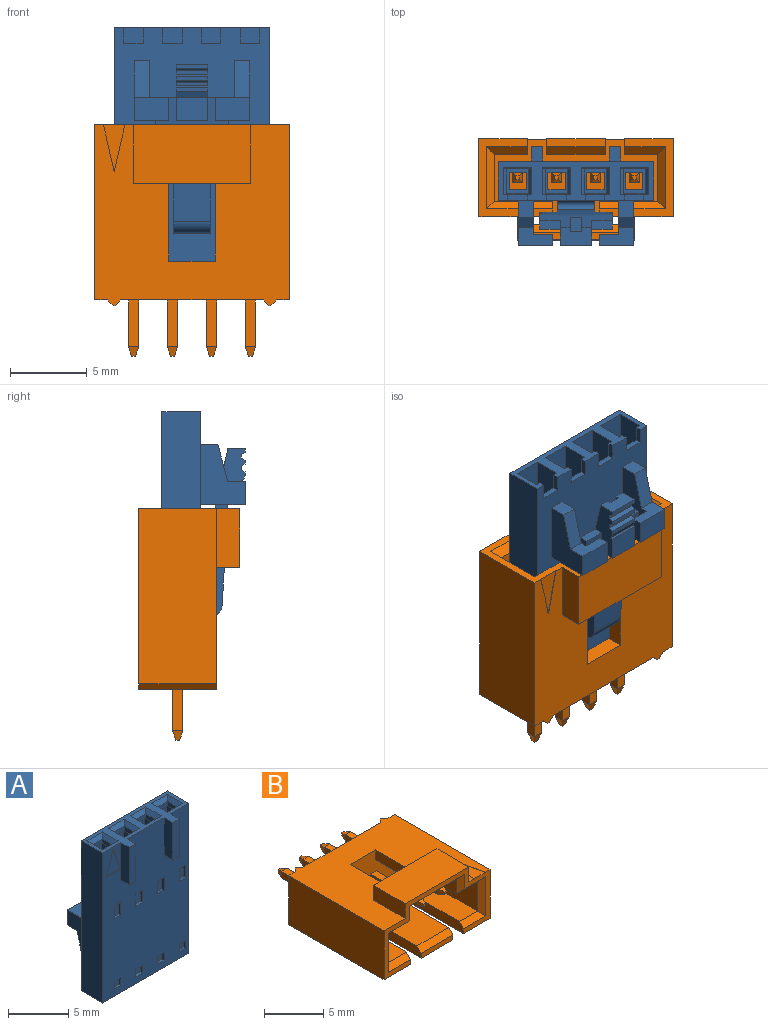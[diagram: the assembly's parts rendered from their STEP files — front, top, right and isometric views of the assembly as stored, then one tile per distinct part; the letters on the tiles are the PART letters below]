
ASSEMBLY  parts=2 mates=1
PART A: 213 faces, bbox 10.1x6.5x15.2 mm
  f0: plane 10.13x2.51mm, normal (0,0,-1), area 10.4mm2, adj f1,f2,f3,f4,f5,f32,f33,f34
  f1: plane 1.02x0.37mm, normal (1,0,0), area 0.4mm2, adj f0,f2,f38,f39
  f2: plane 8.38x1.85mm, normal (0,-1,0), area 14.3mm2, adj f0,f1,f3,f5,f7,f39,f40
  f3: plane 8.38x1.78mm, normal (1,0,0), area 14.9mm2, adj f0,f2,f4,f8
  f4: plane 8.38x1.85mm, normal (0,1,0), area 15.5mm2, adj f0,f3,f5,f9
  f5: plane 8.38x1.78mm, normal (-1,0,0), area 14.9mm2, adj f0,f2,f4,f6
  f6: plane 1.78x0.25mm, normal (-0.76,0,-0.65), area 0.6mm2, adj f5,f7,f9,f11
  f7: plane 1.85x0.25mm, normal (0,-0.96,-0.29), area 0.4mm2, adj f2,f6,f8,f12
  f8: plane 1.78x0.25mm, normal (0.76,0,-0.65), area 0.6mm2, adj f3,f7,f9,f13
  f9: plane 1.85x0.25mm, normal (0,0.96,-0.29), area 0.4mm2, adj f4,f6,f8,f10
  f10: plane 5.79x1.42mm, normal (0,1,0), area 8.2mm2, adj f9,f11,f13,f14
  f11: plane 5.79x1.63mm, normal (-1,0,0), area 9.4mm2, adj f6,f10,f12,f14
  f12: plane 5.79x1.42mm, normal (0,-1,0), area 8.2mm2, adj f7,f11,f13,f14
  f13: plane 5.79x1.63mm, normal (1,0,0), area 9.4mm2, adj f8,f10,f12,f14
  f14: plane 1.63x1.42mm, normal (0,0,-1), area 1.1mm2, adj f10,f11,f12,f13,f15,f16,f17,f18
  f15: plane 1.12x0.46mm, normal (1,0,0), area 0.5mm2, adj f14,f16,f18,f21
  f16: plane 1.12x0.46mm, normal (0,1,0), area 0.5mm2, adj f14,f15,f17,f22
  f17: plane 1.12x0.46mm, normal (-1,0,0), area 0.5mm2, adj f14,f16,f18,f23
  f18: plane 1.12x0.46mm, normal (0,-1,0), area 0.5mm2, adj f14,f15,f17,f19
  f19: plane 1.83x0.36mm, normal (0,-0.71,0.71), area 0.7mm2, adj f18,f20,f21,f23
  f20: plane 10.13x3.53mm, normal (0,0,1), area 13.7mm2, adj f19,f21,f22,f23,f24,f25,f26,f27
  f21: plane 1.83x0.36mm, normal (0.71,0,0.71), area 0.7mm2, adj f15,f19,f20,f22
  f22: plane 1.83x0.36mm, normal (0,0.71,0.71), area 0.7mm2, adj f16,f20,f21,f23
  f23: plane 1.83x0.36mm, normal (-0.71,0,0.71), area 0.7mm2, adj f17,f19,f20,f22
  f24: plane 1.83x0.36mm, normal (0.71,0,0.71), area 0.7mm2, adj f20,f25,f27,f210
  f25: plane 1.83x0.36mm, normal (0,-0.71,0.71), area 0.7mm2, adj f20,f24,f26,f211
  f26: plane 1.83x0.36mm, normal (-0.71,0,0.71), area 0.7mm2, adj f20,f25,f27,f212
  f27: plane 1.83x0.36mm, normal (0,0.71,0.71), area 0.7mm2, adj f20,f24,f26,f28
  f28: plane 1.12x0.46mm, normal (0,1,0), area 0.5mm2, adj f27,f29,f210,f212
  f29: plane 1.63x1.42mm, normal (0,0,-1), area 1.1mm2, adj f28,f30,f205,f206,f209,f210,f211,f212
  f30: plane 5.79x1.63mm, normal (1,0,0), area 9.4mm2, adj f29,f31,f205,f209
  f31: plane 1.78x0.25mm, normal (0.76,0,-0.65), area 0.6mm2, adj f30,f32,f204,f208
  f32: plane 8.38x1.78mm, normal (1,0,0), area 14.9mm2, adj f0,f31,f33,f35
  f33: plane 8.38x1.85mm, normal (0,1,0), area 15.5mm2, adj f0,f32,f34,f208
  f34: plane 8.38x1.78mm, normal (-1,0,0), area 14.9mm2, adj f0,f33,f35,f207
  f35: plane 8.38x1.85mm, normal (0,-1,0), area 14.3mm2, adj f0,f32,f34,f36,f37,f41,f204
  f36: plane 1.02x0.37mm, normal (1,0,0), area 0.4mm2, adj f0,f35,f37,f38
  f37: plane 1.27x0.37mm, normal (0,0,-1), area 0.5mm2, adj f35,f36,f38,f41
  f38: plane 15.24x10.13mm, normal (0,1,0), area 138.1mm2, adj f0,f1,f20,f36,f37,f39,f40,f41
  f39: plane 1.27x0.37mm, normal (0,0,-1), area 0.5mm2, adj f1,f2,f38,f40
  f40: plane 1.02x0.37mm, normal (-1,0,0), area 0.4mm2, adj f0,f2,f38,f39
  f41: plane 1.02x0.37mm, normal (-1,0,0), area 0.4mm2, adj f0,f35,f37,f38
  f42: plane 1.02x0.37mm, normal (1,0,0), area 0.4mm2, adj f0,f38,f43,f65
  f43: plane 8.38x1.85mm, normal (0,-1,0), area 14.3mm2, adj f0,f42,f44,f46,f48,f64,f65
  f44: plane 8.38x1.78mm, normal (1,0,0), area 14.9mm2, adj f0,f43,f45,f49
  f45: plane 8.38x1.85mm, normal (0,1,0), area 15.5mm2, adj f0,f44,f46,f50
  f46: plane 8.38x1.78mm, normal (-1,0,0), area 14.9mm2, adj f0,f43,f45,f47
  f47: plane 1.78x0.25mm, normal (-0.76,0,-0.65), area 0.6mm2, adj f46,f48,f50,f52
  f48: plane 1.85x0.25mm, normal (0,-0.96,-0.29), area 0.4mm2, adj f43,f47,f49,f53
  f49: plane 1.78x0.25mm, normal (0.76,0,-0.65), area 0.6mm2, adj f44,f48,f50,f54
  f50: plane 1.85x0.25mm, normal (0,0.96,-0.29), area 0.4mm2, adj f45,f47,f49,f51
  f51: plane 5.79x1.42mm, normal (0,1,0), area 8.2mm2, adj f50,f52,f54,f55
  f52: plane 5.79x1.63mm, normal (-1,0,0), area 9.4mm2, adj f47,f51,f53,f55
  f53: plane 5.79x1.42mm, normal (0,-1,0), area 8.2mm2, adj f48,f52,f54,f55
  f54: plane 5.79x1.63mm, normal (1,0,0), area 9.4mm2, adj f49,f51,f53,f55
  f55: plane 1.63x1.42mm, normal (0,0,-1), area 1.1mm2, adj f51,f52,f53,f54,f56,f57,f58,f59
  f56: plane 1.12x0.46mm, normal (1,0,0), area 0.5mm2, adj f55,f57,f59,f63
  f57: plane 1.12x0.46mm, normal (0,1,0), area 0.5mm2, adj f55,f56,f58,f62
  f58: plane 1.12x0.46mm, normal (-1,0,0), area 0.5mm2, adj f55,f57,f59,f61
  f59: plane 1.12x0.46mm, normal (0,-1,0), area 0.5mm2, adj f55,f56,f58,f60
  f60: plane 1.83x0.36mm, normal (0,-0.71,0.71), area 0.7mm2, adj f20,f59,f61,f63
  f61: plane 1.83x0.36mm, normal (-0.71,0,0.71), area 0.7mm2, adj f20,f58,f60,f62
  f62: plane 1.83x0.36mm, normal (0,0.71,0.71), area 0.7mm2, adj f20,f57,f61,f63
  f63: plane 1.83x0.36mm, normal (0.71,0,0.71), area 0.7mm2, adj f20,f56,f60,f62
  f64: plane 1.02x0.37mm, normal (-1,0,0), area 0.4mm2, adj f0,f38,f43,f65
  f65: plane 1.27x0.37mm, normal (0,0,-1), area 0.5mm2, adj f38,f42,f43,f64
  f66: plane 1.02x0.37mm, normal (1,0,0), area 0.4mm2, adj f0,f38,f67,f89
  f67: plane 8.38x1.85mm, normal (0,-1,0), area 14.3mm2, adj f0,f66,f68,f70,f72,f88,f89
  f68: plane 8.38x1.78mm, normal (1,0,0), area 14.9mm2, adj f0,f67,f69,f73
  f69: plane 8.38x1.85mm, normal (0,1,0), area 15.5mm2, adj f0,f68,f70,f74
  f70: plane 8.38x1.78mm, normal (-1,0,0), area 14.9mm2, adj f0,f67,f69,f71
  f71: plane 1.78x0.25mm, normal (-0.76,0,-0.65), area 0.6mm2, adj f70,f72,f74,f76
  f72: plane 1.85x0.25mm, normal (0,-0.96,-0.29), area 0.4mm2, adj f67,f71,f73,f77
  f73: plane 1.78x0.25mm, normal (0.76,0,-0.65), area 0.6mm2, adj f68,f72,f74,f78
  f74: plane 1.85x0.25mm, normal (0,0.96,-0.29), area 0.4mm2, adj f69,f71,f73,f75
  f75: plane 5.79x1.42mm, normal (0,1,0), area 8.2mm2, adj f74,f76,f78,f79
  f76: plane 5.79x1.63mm, normal (-1,0,0), area 9.4mm2, adj f71,f75,f77,f79
  f77: plane 5.79x1.42mm, normal (0,-1,0), area 8.2mm2, adj f72,f76,f78,f79
  f78: plane 5.79x1.63mm, normal (1,0,0), area 9.4mm2, adj f73,f75,f77,f79
  f79: plane 1.63x1.42mm, normal (0,0,-1), area 1.1mm2, adj f75,f76,f77,f78,f80,f81,f82,f83
  f80: plane 1.12x0.46mm, normal (1,0,0), area 0.5mm2, adj f79,f81,f83,f87
  f81: plane 1.12x0.46mm, normal (0,1,0), area 0.5mm2, adj f79,f80,f82,f86
  f82: plane 1.12x0.46mm, normal (-1,0,0), area 0.5mm2, adj f79,f81,f83,f85
  f83: plane 1.12x0.46mm, normal (0,-1,0), area 0.5mm2, adj f79,f80,f82,f84
  f84: plane 1.83x0.36mm, normal (0,-0.71,0.71), area 0.7mm2, adj f20,f83,f85,f87
  f85: plane 1.83x0.36mm, normal (-0.71,0,0.71), area 0.7mm2, adj f20,f82,f84,f86
  f86: plane 1.83x0.36mm, normal (0,0.71,0.71), area 0.7mm2, adj f20,f81,f85,f87
  f87: plane 1.83x0.36mm, normal (0.71,0,0.71), area 0.7mm2, adj f20,f80,f84,f86
  f88: plane 1.02x0.37mm, normal (-1,0,0), area 0.4mm2, adj f0,f38,f67,f89
  f89: plane 1.27x0.37mm, normal (0,0,-1), area 0.5mm2, adj f38,f66,f67,f88
  f90: plane 15.24x2.51mm, normal (1,0,0), area 38.3mm2, adj f0,f20,f38,f91
  f91: plane 15.24x10.13mm, normal (0,-1,0), area 140.4mm2, adj f0,f20,f90,f92,f93,f94,f95,f98
  f92: plane 0.76x0.25mm, normal (0,0,1), area 0.2mm2, adj f91,f93,f95,f96
  f93: plane 1.27x0.25mm, normal (1,0,0), area 0.3mm2, adj f91,f92,f94,f96
  f94: plane 0.76x0.25mm, normal (0,0,-1), area 0.2mm2, adj f91,f93,f95,f96
  f95: plane 1.27x0.25mm, normal (-1,0,0), area 0.3mm2, adj f91,f92,f94,f96
  f96: plane 1.27x0.76mm, normal (0,-1,0), area 1mm2, adj f92,f93,f94,f95
  f97: plane 0.76x0.76mm, normal (0,-1,0), area 0.6mm2, adj f98,f99,f100,f101
  f98: plane 0.76x0.25mm, normal (0,0,1), area 0.2mm2, adj f91,f97,f99,f101
  f99: plane 0.76x0.25mm, normal (1,0,0), area 0.2mm2, adj f91,f97,f98,f100
  f100: plane 0.76x0.25mm, normal (0,0,-1), area 0.2mm2, adj f91,f97,f99,f101
  f101: plane 0.76x0.25mm, normal (-1,0,0), area 0.2mm2, adj f91,f97,f98,f100
  f102: plane 0.76x0.25mm, normal (0,0,1), area 0.2mm2, adj f91,f103,f105,f106
  f103: plane 1.27x0.25mm, normal (1,0,0), area 0.3mm2, adj f91,f102,f104,f106
  f104: plane 0.76x0.25mm, normal (0,0,-1), area 0.2mm2, adj f91,f103,f105,f106
  f105: plane 1.27x0.25mm, normal (-1,0,0), area 0.3mm2, adj f91,f102,f104,f106
  f106: plane 1.27x0.76mm, normal (0,-1,0), area 1mm2, adj f102,f103,f104,f105
  f107: plane 0.76x0.76mm, normal (0,-1,0), area 0.6mm2, adj f108,f109,f110,f111
  f108: plane 0.76x0.25mm, normal (0,0,1), area 0.2mm2, adj f91,f107,f109,f111
  f109: plane 0.76x0.25mm, normal (1,0,0), area 0.2mm2, adj f91,f107,f108,f110
  f110: plane 0.76x0.25mm, normal (0,0,-1), area 0.2mm2, adj f91,f107,f109,f111
  f111: plane 0.76x0.25mm, normal (-1,0,0), area 0.2mm2, adj f91,f107,f108,f110
  f112: plane 0.76x0.25mm, normal (0,0,1), area 0.2mm2, adj f91,f113,f115,f116
  f113: plane 1.27x0.25mm, normal (1,0,0), area 0.3mm2, adj f91,f112,f114,f116
  f114: plane 0.76x0.25mm, normal (0,0,-1), area 0.2mm2, adj f91,f113,f115,f116
  f115: plane 1.27x0.25mm, normal (-1,0,0), area 0.3mm2, adj f91,f112,f114,f116
  f116: plane 1.27x0.76mm, normal (0,-1,0), area 1mm2, adj f112,f113,f114,f115
  f117: plane 0.76x0.76mm, normal (0,-1,0), area 0.6mm2, adj f118,f119,f120,f121
  f118: plane 0.76x0.25mm, normal (0,0,1), area 0.2mm2, adj f91,f117,f119,f121
  f119: plane 0.76x0.25mm, normal (1,0,0), area 0.2mm2, adj f91,f117,f118,f120
  f120: plane 0.76x0.25mm, normal (0,0,-1), area 0.2mm2, adj f91,f117,f119,f121
  f121: plane 0.76x0.25mm, normal (-1,0,0), area 0.2mm2, adj f91,f117,f118,f120
  f122: plane 0.76x0.25mm, normal (0,0,1), area 0.2mm2, adj f91,f123,f125,f126
  f123: plane 1.27x0.25mm, normal (1,0,0), area 0.3mm2, adj f91,f122,f124,f126
  f124: plane 0.76x0.25mm, normal (0,0,-1), area 0.2mm2, adj f91,f123,f125,f126
  f125: plane 1.27x0.25mm, normal (-1,0,0), area 0.3mm2, adj f91,f122,f124,f126
  f126: plane 1.27x0.76mm, normal (0,-1,0), area 1mm2, adj f122,f123,f124,f125
  f127: plane 0.76x0.76mm, normal (0,-1,0), area 0.6mm2, adj f128,f129,f130,f131
  f128: plane 0.76x0.25mm, normal (0,0,1), area 0.2mm2, adj f91,f127,f129,f131
  f129: plane 0.76x0.25mm, normal (1,0,0), area 0.2mm2, adj f91,f127,f128,f130
  f130: plane 0.76x0.25mm, normal (0,0,-1), area 0.2mm2, adj f91,f127,f129,f131
  f131: plane 0.76x0.25mm, normal (-1,0,0), area 0.2mm2, adj f91,f127,f128,f130
  f132: plane 3.81x1.02mm, normal (1,0,0), area 3.9mm2, adj f20,f91,f133,f135
  f133: plane 1.02x0.76mm, normal (0,0,-1), area 0.8mm2, adj f91,f132,f134,f135
  f134: plane 3.81x1.02mm, normal (-1,0,0), area 3.9mm2, adj f20,f91,f133,f135
  f135: plane 3.81x0.76mm, normal (0,-1,0), area 2.9mm2, adj f20,f132,f133,f134
  f136: plane 15.24x2.51mm, normal (-1,0,0), area 38.3mm2, adj f0,f20,f38,f91
  f137: plane 3.81x1.02mm, normal (-1,0,0), area 3.9mm2, adj f20,f91,f138,f140
  f138: plane 3.81x0.76mm, normal (0,-1,0), area 2.9mm2, adj f20,f137,f139,f140
  f139: plane 3.81x1.02mm, normal (1,0,0), area 3.9mm2, adj f20,f91,f138,f140
  f140: plane 1.02x0.76mm, normal (0,0,-1), area 0.8mm2, adj f91,f137,f138,f139
  f141: plane 2.54x0.81mm, normal (0.95,0,-0.3), area 0.1mm2, adj f91,f142,f143,f144
  f142: plane 2.54x0.81mm, normal (-0.95,0,-0.3), area 0.1mm2, adj f91,f141,f143,f144
  f143: plane 1.63x0.05mm, normal (0,0,1), area 0.1mm2, adj f91,f141,f142,f144
  f144: plane 2.54x1.63mm, normal (0,-1,0), area 2.1mm2, adj f141,f142,f143
  f145: plane 3.94x2.24mm, normal (-1,0,0), area 6.9mm2, adj f38,f146,f147,f149,f152,f153
  f146: plane 1.52x1.26mm, normal (0,-1,0), area 1.9mm2, adj f145,f147,f149,f150
  f147: plane 2.25x1.14mm, normal (0,0,-1), area 2mm2, adj f145,f146,f148,f150,f151,f152
  f148: plane 2.25x1.52mm, normal (0,1,0), area 3.4mm2, adj f147,f149,f150,f151
  f149: plane 2.92x2.25mm, normal (0,0,1), area 3.8mm2, adj f38,f145,f146,f148,f150,f151
  f150: plane 1.52x0.69mm, normal (-1,0,0), area 1mm2, adj f146,f147,f148,f149
  f151: plane 3.94x2.92mm, normal (1,0,0), area 8mm2, adj f38,f147,f148,f149,f152,f153
  f152: plane 2.41x0.99mm, normal (0,0.97,-0.25), area 2.5mm2, adj f145,f147,f151,f153
  f153: plane 1.14x0.99mm, normal (0,0,-1), area 1.1mm2, adj f38,f145,f151,f152
  f154: plane 3.94x2.24mm, normal (1,0,0), area 6.9mm2, adj f38,f155,f156,f158,f161,f162
  f155: plane 1.52x1.26mm, normal (0,-1,0), area 1.9mm2, adj f154,f156,f158,f159
  f156: plane 2.92x2.25mm, normal (0,0,1), area 3.8mm2, adj f38,f154,f155,f157,f159,f160
  f157: plane 2.25x1.52mm, normal (0,1,0), area 3.4mm2, adj f156,f158,f159,f160
  f158: plane 2.25x1.14mm, normal (0,0,-1), area 2mm2, adj f154,f155,f157,f159,f160,f162
  f159: plane 1.52x0.69mm, normal (1,0,0), area 1mm2, adj f155,f156,f157,f158
  f160: plane 3.94x2.92mm, normal (-1,0,0), area 8mm2, adj f38,f156,f157,f158,f161,f162
  f161: plane 1.14x0.99mm, normal (0,0,-1), area 1.1mm2, adj f38,f154,f160,f162
  f162: plane 2.41x0.99mm, normal (0,0.97,-0.25), area 2.5mm2, adj f154,f158,f160,f161
  f163: plane 4.01x1.6mm, normal (-1,0,0), area 3.9mm2, adj f38,f164,f171,f173,f174,f176,f177
  f164: plane 8.07x4.75mm, normal (0,1,0.06), area 25.1mm2, adj f163,f165,f166,f167,f168,f170,f171,f172
  f165: plane 2.03x0.64mm, normal (0,0,-1), area 1.3mm2, adj f164,f166,f168,f169
  f166: plane 1.22x0.71mm, normal (1,0,0), area 0.6mm2, adj f164,f165,f167,f169
  f167: plane 2.03x0.71mm, normal (0,0.68,0.73), area 2mm2, adj f164,f166,f168,f169
  f168: plane 1.22x0.71mm, normal (-1,0,0), area 0.6mm2, adj f164,f165,f167,f169
  f169: plane 2.03x0.56mm, normal (0,1,0), area 1.1mm2, adj f165,f166,f167,f168
  f170: plane 0.87x0.51mm, normal (-0.71,0,0.71), area 0.6mm2, adj f164,f171,f173,f203
  f171: plane 0.84x0.65mm, normal (0,0,1), area 0.5mm2, adj f163,f164,f170,f173
  f172: plane 0.84x0.65mm, normal (0,0,1), area 0.5mm2, adj f164,f173,f175,f178
  f173: plane 5.94x4.75mm, normal (0,-1,-0.06), area 21.9mm2, adj f163,f170,f171,f172,f174,f175,f178,f179
  f174: cylinder r=0.3mm len=2.44mm, axis (1,0,0), area 2.3mm2, adj f38,f163,f173,f175
  f175: plane 4.01x1.6mm, normal (1,0,0), area 3.9mm2, adj f38,f164,f172,f173,f174,f176,f177
  f176: plane 2.44x0.6mm, normal (0,0,1), area 1.5mm2, adj f38,f163,f175,f177
  f177: cylinder r=0.81mm len=2.44mm, axis (1,0,0), area 3mm2, adj f163,f164,f175,f176
  f178: plane 0.87x0.51mm, normal (0.71,0,0.71), area 0.6mm2, adj f164,f172,f173,f179
  f179: plane 4.32x1.09mm, normal (1,0,0), area 3.4mm2, adj f164,f173,f178,f181,f183
  f180: plane 1.36x0.58mm, normal (0,0,-1), area 0.8mm2, adj f164,f182,f183,f203
  f181: plane 1.36x0.58mm, normal (0,0,-1), area 0.8mm2, adj f164,f179,f183,f189
  f182: plane 3.68x1.62mm, normal (-1,0,0), area 4.4mm2, adj f164,f180,f183,f184,f190,f191,f192,f193
  f183: plane 4.75x3.68mm, normal (0,-0.98,-0.22), area 9.5mm2, adj f173,f179,f180,f181,f182,f184,f185,f187
  f184: plane 2.03x1.13mm, normal (0,0,-1), area 2.1mm2, adj f182,f183,f185,f186,f187,f189,f202
  f185: plane 3.05x0.93mm, normal (-1,0,0), area 1.8mm2, adj f183,f184,f186,f188
  f186: plane 3.05x0.76mm, normal (0,-1,0), area 2.3mm2, adj f184,f185,f187,f188
  f187: plane 3.05x0.93mm, normal (1,0,0), area 1.8mm2, adj f183,f184,f186,f188
  f188: plane 0.93x0.76mm, normal (0,0,-1), area 0.7mm2, adj f183,f185,f186,f187
  f189: plane 3.68x1.62mm, normal (1,0,0), area 4.4mm2, adj f164,f181,f183,f184,f190,f191,f192,f193
  f190: plane 2.03x1.12mm, normal (0,0,1), area 2.3mm2, adj f164,f182,f189,f191
  f191: plane 2.03x1.52mm, normal (0,1,0), area 3.1mm2, adj f182,f189,f190,f192
  f192: plane 2.03x0.19mm, normal (0,0,-1), area 0.4mm2, adj f182,f189,f191,f193
  f193: plane 2.03x0.38mm, normal (0,0.89,0.45), area 0.9mm2, adj f182,f189,f192,f194
  f194: plane 2.03x0.25mm, normal (0,1,0), area 0.5mm2, adj f182,f189,f193,f195
  f195: plane 2.03x0.25mm, normal (0,0.45,-0.89), area 0.6mm2, adj f182,f189,f194,f196
  f196: plane 2.03x0.25mm, normal (0,1,0), area 0.5mm2, adj f182,f189,f195,f197
  f197: plane 2.03x0.25mm, normal (0,0.45,0.89), area 0.6mm2, adj f182,f189,f196,f198
  f198: plane 2.03x0.25mm, normal (0,1,0), area 0.5mm2, adj f182,f189,f197,f199
  f199: plane 2.03x0.25mm, normal (0,0.45,-0.89), area 0.6mm2, adj f182,f189,f198,f200
  f200: plane 2.03x0.25mm, normal (0,1,0), area 0.5mm2, adj f182,f189,f199,f201
  f201: plane 2.03x0.25mm, normal (0,0.45,0.89), area 0.6mm2, adj f182,f189,f200,f202
  f202: plane 2.03x0.25mm, normal (0,1,0), area 0.5mm2, adj f182,f184,f189,f201
  f203: plane 4.32x1.09mm, normal (-1,0,0), area 3.4mm2, adj f164,f170,f173,f180,f183
  f204: plane 1.85x0.25mm, normal (0,-0.96,-0.29), area 0.4mm2, adj f31,f35,f205,f207
  f205: plane 5.79x1.42mm, normal (0,-1,0), area 8.2mm2, adj f29,f30,f204,f206
  f206: plane 5.79x1.63mm, normal (-1,0,0), area 9.4mm2, adj f29,f205,f207,f209
  f207: plane 1.78x0.25mm, normal (-0.76,0,-0.65), area 0.6mm2, adj f34,f204,f206,f208
  f208: plane 1.85x0.25mm, normal (0,0.96,-0.29), area 0.4mm2, adj f31,f33,f207,f209
  f209: plane 5.79x1.42mm, normal (0,1,0), area 8.2mm2, adj f29,f30,f206,f208
  f210: plane 1.12x0.46mm, normal (1,0,0), area 0.5mm2, adj f24,f28,f29,f211
  f211: plane 1.12x0.46mm, normal (0,-1,0), area 0.5mm2, adj f25,f29,f210,f212
  f212: plane 1.12x0.46mm, normal (-1,0,0), area 0.5mm2, adj f26,f28,f29,f211
PART B: 125 faces, bbox 12.7x15.1x6.6 mm
  f0: plane 11.43x5.08mm, normal (-1,0,0), area 58.1mm2, adj f1,f4,f24,f28
  f1: plane 12.7x11.81mm, normal (0,0,1), area 98.9mm2, adj f0,f2,f4,f6,f24,f25,f26,f27
  f2: plane 3.05x0.7mm, normal (-0.97,-0.22,0), area 0.1mm2, adj f1,f4,f123,f124
  f3: plane 3.81x0.51mm, normal (0,-1,0), area 1.9mm2, adj f5,f28,f29,f31
  f4: plane 12.7x6.6mm, normal (0,-1,0), area 15.3mm2, adj f0,f1,f2,f28,f30,f32,f33,f38
  f5: plane 8.89x1.02mm, normal (-1,0,0), area 8.9mm2, adj f3,f6,f28,f31,f35
  f6: plane 10.67x5.08mm, normal (0,-1,0), area 36.4mm2, adj f1,f5,f7,f9,f15,f17,f28,f29
  f7: plane 5.46x0.66mm, normal (-1,0,0), area 3.6mm2, adj f6,f9,f15,f122
  f8: plane 3.05x0.66mm, normal (-1,0,0), area 2mm2, adj f10,f16,f22,f25
  f9: plane 5.46x0.66mm, normal (0,0,1), area 3.6mm2, adj f6,f7,f11,f17
  f10: plane 3.05x0.66mm, normal (0,0,1), area 2mm2, adj f8,f18,f21,f25
  f11: plane 0.66x0.64mm, normal (0,-0.3,0.95), area 0.3mm2, adj f9,f12,f13,f122
  f12: plane 0.66x0.64mm, normal (0.95,-0.3,0), area 0.3mm2, adj f11,f13,f14,f17
  f13: plane 0.25x0.25mm, normal (0,-1,0), area 0.1mm2, adj f11,f12,f14,f122
  f14: plane 0.66x0.64mm, normal (0,-0.3,-0.95), area 0.3mm2, adj f12,f13,f15,f122
  f15: plane 5.46x0.66mm, normal (0,0,-1), area 3.6mm2, adj f6,f7,f14,f17
  f16: plane 3.05x0.66mm, normal (0,0,-1), area 2mm2, adj f8,f18,f23,f25
  f17: plane 5.46x0.66mm, normal (1,0,0), area 3.6mm2, adj f6,f9,f12,f15
  f18: plane 3.05x0.66mm, normal (1,0,0), area 2mm2, adj f10,f16,f19,f25
  f19: plane 0.66x0.64mm, normal (0.95,0.3,0), area 0.3mm2, adj f18,f20,f21,f23
  f20: plane 0.25x0.25mm, normal (0,1,0), area 0.1mm2, adj f19,f21,f22,f23
  f21: plane 0.66x0.64mm, normal (0,0.3,0.95), area 0.3mm2, adj f10,f19,f20,f22
  f22: plane 0.66x0.64mm, normal (-0.95,0.3,0), area 0.3mm2, adj f8,f20,f21,f23
  f23: plane 0.66x0.64mm, normal (0,0.3,-0.95), area 0.3mm2, adj f16,f19,f20,f22
  f24: plane 5.08x0.83mm, normal (0,1,0), area 4.2mm2, adj f0,f1,f27,f28
  f25: plane 9.27x5.08mm, normal (0,1,0), area 45.4mm2, adj f1,f8,f10,f16,f18,f28,f65,f66
  f26: plane 5.08x0.83mm, normal (0,1,0), area 4.2mm2, adj f1,f28,f62,f63
  f27: plane 5.08x0.38mm, normal (-0.71,0.71,0), area 2.7mm2, adj f1,f24,f28,f67
  f28: plane 12.7x11.81mm, normal (0,0,-1), area 123mm2, adj f0,f3,f4,f5,f6,f24,f25,f26
  f29: plane 8.89x1.02mm, normal (1,0,0), area 8.9mm2, adj f3,f6,f28,f31,f35
  f30: plane 2.67x0.51mm, normal (0,-0.71,0.71), area 1.7mm2, adj f4,f33,f34,f38
  f31: plane 3.81x0.51mm, normal (0,-0.71,0.71), area 2.7mm2, adj f3,f5,f29,f35
  f32: plane 2.67x0.51mm, normal (0,-0.71,0.71), area 1.7mm2, adj f4,f36,f47,f61
  f33: plane 8.89x1.02mm, normal (-1,0,0), area 8.9mm2, adj f4,f6,f28,f30,f34
  f34: plane 8.38x2.16mm, normal (0,0,1), area 18.1mm2, adj f6,f30,f33,f37
  f35: plane 8.38x3.81mm, normal (0,0,1), area 31.9mm2, adj f5,f6,f29,f31
  f36: plane 8.38x2.16mm, normal (0,0,1), area 18.1mm2, adj f6,f32,f46,f61
  f37: plane 8.38x3.05mm, normal (-1,0,0), area 25.5mm2, adj f6,f34,f38,f40
  f38: plane 4.06x0.51mm, normal (-0.71,-0.71,0), area 2.6mm2, adj f4,f30,f37,f39
  f39: plane 3.05x0.51mm, normal (0,-0.71,-0.71), area 1.8mm2, adj f4,f38,f40,f60
  f40: plane 8.38x3.81mm, normal (0,0,-1), area 27.1mm2, adj f6,f37,f39,f41,f52,f53
  f41: plane 5.08x1.02mm, normal (-1,0,0), area 5mm2, adj f1,f6,f40,f43,f53
  f42: plane 1.27x0.51mm, normal (0,-1,0), area 0.6mm2, adj f1,f44,f58,f59
  f43: plane 1.27x0.51mm, normal (0,-1,0), area 0.6mm2, adj f1,f41,f52,f53
  f44: plane 5.08x1.02mm, normal (1,0,0), area 5mm2, adj f1,f6,f42,f45,f59
  f45: plane 8.38x3.81mm, normal (0,0,-1), area 27.1mm2, adj f6,f44,f46,f48,f58,f59
  f46: plane 8.38x3.05mm, normal (1,0,0), area 25.5mm2, adj f6,f36,f45,f47
  f47: plane 4.06x0.51mm, normal (0.71,-0.71,0), area 2.6mm2, adj f4,f32,f46,f48
  f48: plane 3.05x0.51mm, normal (0,-0.71,-0.71), area 1.8mm2, adj f4,f45,f47,f49
  f49: plane 2.03x0.51mm, normal (0.71,-0.71,0), area 1.1mm2, adj f4,f48,f50,f58
  f50: plane 6.6x0.51mm, normal (0,-0.71,-0.71), area 4.4mm2, adj f4,f49,f51,f60
  f51: plane 5.59x3.3mm, normal (0,0,-1), area 18.5mm2, adj f50,f52,f54,f58
  f52: plane 3.81x1.52mm, normal (-1,0,0), area 5.2mm2, adj f40,f43,f51,f53,f54,f60
  f53: plane 1.27x0.51mm, normal (0,-0.71,-0.71), area 0.9mm2, adj f40,f41,f43,f52
  f54: plane 7.62x1.52mm, normal (0,1,0), area 8.8mm2, adj f1,f51,f52,f55,f56,f57,f58
  f55: plane 3.81x1.52mm, normal (1,0,0), area 5.8mm2, adj f1,f4,f54,f56
  f56: plane 7.62x3.81mm, normal (0,0,1), area 29mm2, adj f4,f54,f55,f57
  f57: plane 3.81x1.52mm, normal (-1,0,0), area 5.8mm2, adj f1,f4,f54,f56
  f58: plane 3.81x1.52mm, normal (1,0,0), area 5.2mm2, adj f42,f45,f49,f51,f54,f59
  f59: plane 1.27x0.51mm, normal (0,-0.71,-0.71), area 0.9mm2, adj f42,f44,f45,f58
  f60: plane 2.03x0.51mm, normal (-0.71,-0.71,0), area 1.1mm2, adj f4,f39,f50,f52
  f61: plane 8.89x1.02mm, normal (1,0,0), area 8.9mm2, adj f4,f6,f28,f32,f36
  f62: plane 11.43x5.08mm, normal (1,0,0), area 58.1mm2, adj f1,f4,f26,f28
  f63: plane 5.08x0.38mm, normal (0.71,0.71,0), area 2.7mm2, adj f1,f26,f28,f64
  f64: plane 5.08x0.13mm, normal (0,1,0), area 0.6mm2, adj f1,f28,f63,f65
  f65: plane 5.08x0.38mm, normal (-0.71,0.71,0), area 2.7mm2, adj f1,f25,f28,f64
  f66: plane 5.08x0.38mm, normal (0.71,0.71,0), area 2.7mm2, adj f1,f25,f28,f67
  f67: plane 5.08x0.13mm, normal (0,1,0), area 0.6mm2, adj f1,f27,f28,f66
  f68: plane 5.46x0.66mm, normal (-1,0,0), area 3.6mm2, adj f6,f70,f73,f79
  f69: plane 3.05x0.66mm, normal (-1,0,0), area 2mm2, adj f25,f74,f80,f85
  f70: plane 0.66x0.64mm, normal (-0.95,-0.3,0), area 0.3mm2, adj f68,f71,f72,f78
  f71: plane 0.25x0.25mm, normal (0,-1,0), area 0.1mm2, adj f70,f72,f77,f78
  f72: plane 0.66x0.64mm, normal (0,-0.3,0.95), area 0.3mm2, adj f70,f71,f73,f77
  f73: plane 5.46x0.66mm, normal (0,0,1), area 3.6mm2, adj f6,f68,f72,f75
  f74: plane 3.05x0.66mm, normal (0,0,1), area 2mm2, adj f25,f69,f76,f84
  f75: plane 5.46x0.66mm, normal (1,0,0), area 3.6mm2, adj f6,f73,f77,f79
  f76: plane 3.05x0.66mm, normal (1,0,0), area 2mm2, adj f25,f74,f80,f82
  f77: plane 0.66x0.64mm, normal (0.95,-0.3,0), area 0.3mm2, adj f71,f72,f75,f78
  f78: plane 0.66x0.64mm, normal (0,-0.3,-0.95), area 0.3mm2, adj f70,f71,f77,f79
  f79: plane 5.46x0.66mm, normal (0,0,-1), area 3.6mm2, adj f6,f68,f75,f78
  f80: plane 3.05x0.66mm, normal (0,0,-1), area 2mm2, adj f25,f69,f76,f81
  f81: plane 0.66x0.64mm, normal (0,0.3,-0.95), area 0.3mm2, adj f80,f82,f83,f85
  f82: plane 0.66x0.64mm, normal (0.95,0.3,0), area 0.3mm2, adj f76,f81,f83,f84
  f83: plane 0.25x0.25mm, normal (0,1,0), area 0.1mm2, adj f81,f82,f84,f85
  f84: plane 0.66x0.64mm, normal (0,0.3,0.95), area 0.3mm2, adj f74,f82,f83,f85
  f85: plane 0.66x0.64mm, normal (-0.95,0.3,0), area 0.3mm2, adj f69,f81,f83,f84
  f86: plane 5.46x0.66mm, normal (-1,0,0), area 3.6mm2, adj f6,f88,f91,f97
  f87: plane 3.05x0.66mm, normal (-1,0,0), area 2mm2, adj f25,f92,f98,f103
  f88: plane 0.66x0.64mm, normal (-0.95,-0.3,0), area 0.3mm2, adj f86,f89,f90,f96
  f89: plane 0.25x0.25mm, normal (0,-1,0), area 0.1mm2, adj f88,f90,f95,f96
  f90: plane 0.66x0.64mm, normal (0,-0.3,0.95), area 0.3mm2, adj f88,f89,f91,f95
  f91: plane 5.46x0.66mm, normal (0,0,1), area 3.6mm2, adj f6,f86,f90,f93
  f92: plane 3.05x0.66mm, normal (0,0,1), area 2mm2, adj f25,f87,f94,f102
  f93: plane 5.46x0.66mm, normal (1,0,0), area 3.6mm2, adj f6,f91,f95,f97
  f94: plane 3.05x0.66mm, normal (1,0,0), area 2mm2, adj f25,f92,f98,f100
  f95: plane 0.66x0.64mm, normal (0.95,-0.3,0), area 0.3mm2, adj f89,f90,f93,f96
  f96: plane 0.66x0.64mm, normal (0,-0.3,-0.95), area 0.3mm2, adj f88,f89,f95,f97
  f97: plane 5.46x0.66mm, normal (0,0,-1), area 3.6mm2, adj f6,f86,f93,f96
  f98: plane 3.05x0.66mm, normal (0,0,-1), area 2mm2, adj f25,f87,f94,f99
  f99: plane 0.66x0.64mm, normal (0,0.3,-0.95), area 0.3mm2, adj f98,f100,f101,f103
  f100: plane 0.66x0.64mm, normal (0.95,0.3,0), area 0.3mm2, adj f94,f99,f101,f102
  f101: plane 0.25x0.25mm, normal (0,1,0), area 0.1mm2, adj f99,f100,f102,f103
  f102: plane 0.66x0.64mm, normal (0,0.3,0.95), area 0.3mm2, adj f92,f100,f101,f103
  f103: plane 0.66x0.64mm, normal (-0.95,0.3,0), area 0.3mm2, adj f87,f99,f101,f102
  f104: plane 5.46x0.66mm, normal (-1,0,0), area 3.6mm2, adj f6,f106,f109,f115
  f105: plane 3.05x0.66mm, normal (-1,0,0), area 2mm2, adj f25,f110,f116,f121
  f106: plane 0.66x0.64mm, normal (-0.95,-0.3,0), area 0.3mm2, adj f104,f107,f108,f114
  f107: plane 0.25x0.25mm, normal (0,-1,0), area 0.1mm2, adj f106,f108,f113,f114
  f108: plane 0.66x0.64mm, normal (0,-0.3,0.95), area 0.3mm2, adj f106,f107,f109,f113
  f109: plane 5.46x0.66mm, normal (0,0,1), area 3.6mm2, adj f6,f104,f108,f111
  f110: plane 3.05x0.66mm, normal (0,0,1), area 2mm2, adj f25,f105,f112,f120
  f111: plane 5.46x0.66mm, normal (1,0,0), area 3.6mm2, adj f6,f109,f113,f115
  f112: plane 3.05x0.66mm, normal (1,0,0), area 2mm2, adj f25,f110,f116,f118
  f113: plane 0.66x0.64mm, normal (0.95,-0.3,0), area 0.3mm2, adj f107,f108,f111,f114
  f114: plane 0.66x0.64mm, normal (0,-0.3,-0.95), area 0.3mm2, adj f106,f107,f113,f115
  f115: plane 5.46x0.66mm, normal (0,0,-1), area 3.6mm2, adj f6,f104,f111,f114
  f116: plane 3.05x0.66mm, normal (0,0,-1), area 2mm2, adj f25,f105,f112,f117
  f117: plane 0.66x0.64mm, normal (0,0.3,-0.95), area 0.3mm2, adj f116,f118,f119,f121
  f118: plane 0.66x0.64mm, normal (0.95,0.3,0), area 0.3mm2, adj f112,f117,f119,f120
  f119: plane 0.25x0.25mm, normal (0,1,0), area 0.1mm2, adj f117,f118,f120,f121
  f120: plane 0.66x0.64mm, normal (0,0.3,0.95), area 0.3mm2, adj f110,f118,f119,f121
  f121: plane 0.66x0.64mm, normal (-0.95,0.3,0), area 0.3mm2, adj f105,f117,f119,f120
  f122: plane 0.66x0.64mm, normal (-0.95,-0.3,0), area 0.3mm2, adj f7,f11,f13,f14
  f123: plane 3.05x1.4mm, normal (0,0,1), area 2.1mm2, adj f2,f4,f124
  f124: plane 3.05x0.7mm, normal (0.97,-0.22,0), area 0.1mm2, adj f1,f2,f4,f123
PLACE A rot(axis=(1,0,0),180deg) t=(-6.35,-2.77,10.16)mm
PLACE B rot(axis=(0,-0.71,0.71),180deg) t=(-6.35,-2.54,7.62)mm
MATE fastened A.f20 <-> B.f6  axis (0,0,-1) through (-6.35,-2.57,2.54)mm
